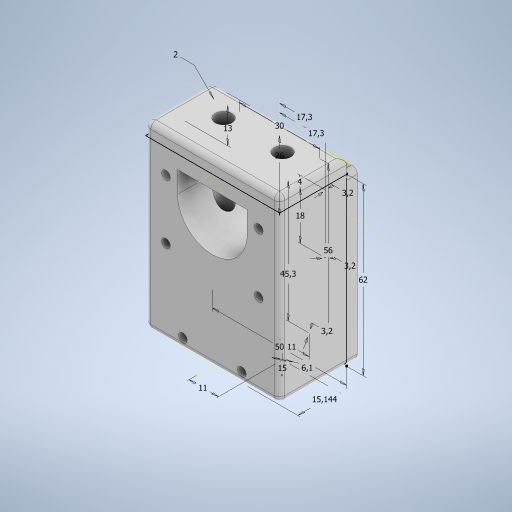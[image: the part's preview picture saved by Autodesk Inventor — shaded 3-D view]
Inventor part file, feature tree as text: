
AUTODESK INVENTOR PART (.ipt)
format: ipt  version: 2024.3 (Build 283343000, 343)  size: 379,904 bytes
history: native  units: mm
features: extrude x5, sketch x3, other x1, fillet x1, hole x1
ambient origin geometry x8: Origin, YZ Plane, XZ Plane, XY Plane, X Axis, Y Axis, Z Axis, Center Point
bodies: Body1 (feature_tree)
feature tree (11):
  other  "Bryła1"
  sketch  "Szkic1"
  extrude  "Wyciągnięcie proste1"  Depth=50.0mm
  extrude  "Wyciągnięcie proste2"  Depth=62.0mm
  sketch  "Szkic2"
  extrude  "Wyciągnięcie proste4"  Depth=13.0mm
  sketch  "Szkic3"
  extrude  "Wyciągnięcie proste6"  Depth=3.2mm
  extrude  "Wyciągnięcie proste7"  Depth=3.2mm
  fillet  "Zaokrąglenie1"  Radius=3.2mm
  hole  "Otwór1"  [1 undecoded]
note: 1 required parameter value undecoded (feature->parameter linkage not recoverable at this tier; creation-order binding heuristic only, values carry confidence <= 0.55)
